AUTODESK INVENTOR PART (.ipt)
format: ipt  version: 2016 SP2 (Build 200236200, 236)  size: 8,607,232 bytes
history: native  units: mm
features: sketch x1
ambient origin geometry x8: Origin, YZ Plane, XZ Plane, XY Plane, X Axis, Y Axis, Z Axis, Center Point
bodies: Solid1 (feature_tree), Solid2 (feature_tree), Solid3 (feature_tree), Solid4 (feature_tree), Solid5 (feature_tree), Solid6 (feature_tree), Solid7 (feature_tree), Solid8 (feature_tree), Solid9 (feature_tree), Solid10 (feature_tree), Solid11 (feature_tree), Solid12 (feature_tree), Solid13 (feature_tree), Solid14 (feature_tree), Solid15 (feature_tree), Solid16 (feature_tree), Solid17 (feature_tree), Solid18 (feature_tree), Solid19 (feature_tree), Solid20 (feature_tree), Solid21 (feature_tree), Solid22 (feature_tree), Solid23 (feature_tree), Solid24 (feature_tree), Solid25 (feature_tree), Solid26 (feature_tree), Solid27 (feature_tree), Solid28 (feature_tree), Solid29 (feature_tree), Solid30 (feature_tree), Solid31 (feature_tree), Solid32 (feature_tree), Solid33 (feature_tree), Solid34 (feature_tree), Solid35 (feature_tree), Solid36 (feature_tree), Solid37 (feature_tree), Solid38 (feature_tree), Solid39 (feature_tree), Solid40 (feature_tree), Solid41 (feature_tree), Solid42 (feature_tree), Solid43 (feature_tree), Solid44 (feature_tree), Solid45 (feature_tree), Solid46 (feature_tree), Solid47 (feature_tree), Solid48 (feature_tree), Solid49 (feature_tree), Solid50 (feature_tree), Solid51 (feature_tree), Solid52 (feature_tree), Solid53 (feature_tree), Solid54 (feature_tree), Solid55 (feature_tree), Solid56 (feature_tree), Solid57 (feature_tree), Solid58 (feature_tree), Solid59 (feature_tree), Solid60 (feature_tree), Solid61 (feature_tree), Solid62 (feature_tree), Solid63 (feature_tree), Solid64 (feature_tree), Solid65 (feature_tree), Solid66 (feature_tree), Solid67 (feature_tree), Solid68 (feature_tree), Solid69 (feature_tree), Solid70 (feature_tree), Solid71 (feature_tree), Solid72 (feature_tree), Solid73 (feature_tree), Solid74 (feature_tree), Solid75 (feature_tree), Solid76 (feature_tree), Solid77 (feature_tree), Solid78 (feature_tree), Solid79 (feature_tree), Solid80 (feature_tree), Solid81 (feature_tree), Solid82 (feature_tree), Solid83 (feature_tree), Solid84 (feature_tree), Solid85 (feature_tree), Solid86 (feature_tree), Solid87 (feature_tree), Solid88 (feature_tree), Solid89 (feature_tree), Solid90 (feature_tree), Solid91 (feature_tree), Solid92 (feature_tree), Solid93 (feature_tree), Solid94 (feature_tree), Solid95 (feature_tree), Solid96 (feature_tree), Solid97 (feature_tree), Solid98 (feature_tree), Solid99 (feature_tree), Solid100 (feature_tree), Solid101 (feature_tree), Solid102 (feature_tree), Solid103 (feature_tree), Solid104 (feature_tree), Solid105 (feature_tree), Solid106 (feature_tree), Solid107 (feature_tree), Solid108 (feature_tree), Solid109 (feature_tree), Solid110 (feature_tree), Solid111 (feature_tree), Solid112 (feature_tree), Solid113 (feature_tree), Solid114 (feature_tree), Solid115 (feature_tree), Solid116 (feature_tree), Solid117 (feature_tree), Solid118 (feature_tree), Solid119 (feature_tree), Solid120 (feature_tree), Solid121 (feature_tree), Solid122 (feature_tree), Solid123 (feature_tree), Solid124 (feature_tree), Solid125 (feature_tree), Solid126 (feature_tree), Solid127 (feature_tree), Solid128 (feature_tree), Solid129 (feature_tree), Solid130 (feature_tree), Solid131 (feature_tree), Solid132 (feature_tree), Solid133 (feature_tree), Solid134 (feature_tree), Solid135 (feature_tree), Solid136 (feature_tree), Solid137 (feature_tree), Solid138 (feature_tree), Solid139 (feature_tree), Solid140 (feature_tree), Solid141 (feature_tree), Solid142 (feature_tree), Solid143 (feature_tree), Solid144 (feature_tree), Solid145 (feature_tree), Solid146 (feature_tree), Solid147 (feature_tree), Solid148 (feature_tree), Solid149 (feature_tree), Solid150 (feature_tree), Solid151 (feature_tree), Solid152 (feature_tree), Solid153 (feature_tree), Solid154 (feature_tree), Solid155 (feature_tree), Solid156 (feature_tree), Solid157 (feature_tree), Solid158 (feature_tree), Solid159 (feature_tree), Solid160 (feature_tree), Solid161 (feature_tree), Solid162 (feature_tree), Solid163 (feature_tree), Solid164 (feature_tree), Solid165 (feature_tree), Solid166 (feature_tree), Solid167 (feature_tree), Solid168 (feature_tree), Solid169 (feature_tree), Solid170 (feature_tree), Solid171 (feature_tree), Solid172 (feature_tree), Solid173 (feature_tree), Solid174 (feature_tree), Solid175 (feature_tree), Solid176 (feature_tree), Solid177 (feature_tree), Solid178 (feature_tree), Solid179 (feature_tree), Solid180 (feature_tree), Solid181 (feature_tree), Solid182 (feature_tree), Solid183 (feature_tree), Solid184 (feature_tree), Solid185 (feature_tree), Solid186 (feature_tree), Solid187 (feature_tree), Solid188 (feature_tree), Solid189 (feature_tree), Solid190 (feature_tree), Solid191 (feature_tree), Solid192 (feature_tree), Solid193 (feature_tree), Solid194 (feature_tree), Solid195 (feature_tree), Solid196 (feature_tree), Solid197 (feature_tree), Solid198 (feature_tree), Solid199 (feature_tree), Solid200 (feature_tree), Solid201 (feature_tree), Solid202 (feature_tree), Solid203 (feature_tree), Solid204 (feature_tree), Solid205 (feature_tree), Solid206 (feature_tree), Solid207 (feature_tree), Solid208 (feature_tree), Solid209 (feature_tree), Solid210 (feature_tree), Solid211 (feature_tree), Solid212 (feature_tree), Solid213 (feature_tree), Solid214 (feature_tree), Solid215 (feature_tree), Solid216 (feature_tree), Solid217 (feature_tree), Solid218 (feature_tree), Solid219 (feature_tree), Solid220 (feature_tree), Solid221 (feature_tree), Solid222 (feature_tree), Solid223 (feature_tree), Solid224 (feature_tree), Solid225 (feature_tree), Solid226 (feature_tree), Solid227 (feature_tree), Solid228 (feature_tree), Solid229 (feature_tree), Solid230 (feature_tree), Solid231 (feature_tree), Solid232 (feature_tree), Solid233 (feature_tree), Solid234 (feature_tree), Solid235 (feature_tree), Solid236 (feature_tree), Solid237 (feature_tree), Solid238 (feature_tree), Solid239 (feature_tree), Solid240 (feature_tree), Solid241 (feature_tree), Solid242 (feature_tree), Solid243 (feature_tree), Solid244 (feature_tree), Solid245 (feature_tree), Solid246 (feature_tree), Solid247 (feature_tree), Solid248 (feature_tree), Solid249 (feature_tree), Solid250 (feature_tree), Solid251 (feature_tree), Solid252 (feature_tree), Solid253 (feature_tree), Solid254 (feature_tree), Solid255 (feature_tree), Solid256 (feature_tree), Solid257 (feature_tree), Solid258 (feature_tree), Solid259 (feature_tree), Solid260 (feature_tree), Solid261 (feature_tree), Solid262 (feature_tree), Solid263 (feature_tree), Solid264 (feature_tree), Solid265 (feature_tree), Solid266 (feature_tree), Solid267 (feature_tree), Solid268 (feature_tree), Solid269 (feature_tree), Solid270 (feature_tree), Solid271 (feature_tree), Solid272 (feature_tree), Solid273 (feature_tree), Solid274 (feature_tree), Solid275 (feature_tree), Solid276 (feature_tree), Solid277 (feature_tree), Solid278 (feature_tree), Solid279 (feature_tree), Solid280 (feature_tree), Solid281 (feature_tree), Solid282 (feature_tree), Solid283 (feature_tree), Solid284 (feature_tree), Solid285 (feature_tree), Solid286 (feature_tree), Solid287 (feature_tree), Solid288 (feature_tree), Solid289 (feature_tree), Solid290 (feature_tree), Solid291 (feature_tree), Solid292 (feature_tree), Solid293 (feature_tree), Solid294 (feature_tree), Solid295 (feature_tree), Solid296 (feature_tree), Solid297 (feature_tree), Solid298 (feature_tree), Solid299 (feature_tree), Solid300 (feature_tree), Solid301 (feature_tree), Solid302 (feature_tree), Solid303 (feature_tree), Solid304 (feature_tree), Solid305 (feature_tree), Solid306 (feature_tree), Solid307 (feature_tree), Solid308 (feature_tree), Solid309 (feature_tree), Solid310 (feature_tree), Solid311 (feature_tree), Solid312 (feature_tree), Solid313 (feature_tree), Solid314 (feature_tree), Solid315 (feature_tree), Solid316 (feature_tree), Solid317 (feature_tree), Solid318 (feature_tree), Solid319 (feature_tree), Solid320 (feature_tree), Solid321 (feature_tree), Solid322 (feature_tree), Solid323 (feature_tree), Solid324 (feature_tree), Solid325 (feature_tree), Solid326 (feature_tree), Solid327 (feature_tree), Solid328 (feature_tree), Solid329 (feature_tree), Solid330 (feature_tree), Solid331 (feature_tree), Solid332 (feature_tree), Solid333 (feature_tree), Solid334 (feature_tree), Solid335 (feature_tree), Solid336 (feature_tree), Solid337 (feature_tree), Solid338 (feature_tree), Solid339 (feature_tree), Solid340 (feature_tree), Solid341 (feature_tree), Solid342 (feature_tree), Solid343 (feature_tree), Solid344 (feature_tree), Solid345 (feature_tree), Solid346 (feature_tree), Solid347 (feature_tree), Solid348 (feature_tree), Solid349 (feature_tree), Solid350 (feature_tree), Solid351 (feature_tree), Solid352 (feature_tree), Solid353 (feature_tree), Solid354 (feature_tree), Solid355 (feature_tree), Solid356 (feature_tree), Solid357 (feature_tree), Solid358 (feature_tree), Solid359 (feature_tree), Solid360 (feature_tree), Solid361 (feature_tree), Solid362 (feature_tree), Solid363 (feature_tree), Solid364 (feature_tree), Solid365 (feature_tree), Solid366 (feature_tree), Solid367 (feature_tree), Solid368 (feature_tree), Solid369 (feature_tree), Solid370 (feature_tree), Solid371 (feature_tree), Solid372 (feature_tree), Solid373 (feature_tree), Solid374 (feature_tree), Solid375 (feature_tree), Solid376 (feature_tree), Solid377 (feature_tree), Solid378 (feature_tree), Solid379 (feature_tree), Solid380 (feature_tree), Solid381 (feature_tree), Solid382 (feature_tree), Solid383 (feature_tree), Solid384 (feature_tree), Solid385 (feature_tree), Solid386 (feature_tree), Solid387 (feature_tree), Solid388 (feature_tree), Solid389 (feature_tree), Solid390 (feature_tree), Solid391 (feature_tree), Solid392 (feature_tree), Solid393 (feature_tree), Solid394 (feature_tree), Solid395 (feature_tree), Solid396 (feature_tree), Solid397 (feature_tree), Solid398 (feature_tree), Solid399 (feature_tree), Solid400 (feature_tree), Solid401 (feature_tree), Solid402 (feature_tree), Solid403 (feature_tree), Solid404 (feature_tree), Solid405 (feature_tree), Solid406 (feature_tree), Solid407 (feature_tree), Solid408 (feature_tree), Solid409 (feature_tree), Solid410 (feature_tree), Solid411 (feature_tree), Solid412 (feature_tree), Solid413 (feature_tree), Solid414 (feature_tree), Solid415 (feature_tree), Solid416 (feature_tree), Solid417 (feature_tree), Solid418 (feature_tree), Solid419 (feature_tree), Solid420 (feature_tree), Solid421 (feature_tree), Solid422 (feature_tree), Solid423 (feature_tree), Solid424 (feature_tree), Solid425 (feature_tree), Solid426 (feature_tree), Solid427 (feature_tree), Solid428 (feature_tree), Solid429 (feature_tree), Solid430 (feature_tree), Solid431 (feature_tree), Solid432 (feature_tree), Solid433 (feature_tree), Solid434 (feature_tree), Solid435 (feature_tree), Solid436 (feature_tree), Solid437 (feature_tree), Solid438 (feature_tree), Solid439 (feature_tree), Solid440 (feature_tree), Solid441 (feature_tree), Solid442 (feature_tree), Solid443 (feature_tree), Solid444 (feature_tree), Solid445 (feature_tree), Solid446 (feature_tree), Solid447 (feature_tree), Solid448 (feature_tree), Solid449 (feature_tree), Solid450 (feature_tree), Solid451 (feature_tree), Solid452 (feature_tree), Solid453 (feature_tree), Solid454 (feature_tree), Solid455 (feature_tree), Solid456 (feature_tree), Solid457 (feature_tree), Solid458 (feature_tree), Solid459 (feature_tree), Solid460 (feature_tree), Solid461 (feature_tree), Solid462 (feature_tree), Solid463 (feature_tree), Solid464 (feature_tree), Solid465 (feature_tree), Solid466 (feature_tree), Solid467 (feature_tree), Solid468 (feature_tree), Solid469 (feature_tree), Solid470 (feature_tree), Solid471 (feature_tree), Solid472 (feature_tree), Solid473 (feature_tree), Solid474 (feature_tree), Solid475 (feature_tree), Solid476 (feature_tree), Solid477 (feature_tree), Solid478 (feature_tree), Solid479 (feature_tree), Solid480 (feature_tree), Solid481 (feature_tree), Solid482 (feature_tree), Solid483 (feature_tree), Solid484 (feature_tree), Solid485 (feature_tree), Solid486 (feature_tree), Solid487 (feature_tree), Solid488 (feature_tree), Solid489 (feature_tree), Solid490 (feature_tree), Solid491 (feature_tree), Solid492 (feature_tree), Solid493 (feature_tree), Solid494 (feature_tree), Solid495 (feature_tree), Solid496 (feature_tree), Solid497 (feature_tree), Solid498 (feature_tree), Solid499 (feature_tree), Solid500 (feature_tree), Solid501 (feature_tree), Solid502 (feature_tree), Solid503 (feature_tree), Solid504 (feature_tree), Solid505 (feature_tree), Solid506 (feature_tree), Solid507 (feature_tree), Solid508 (feature_tree), Solid509 (feature_tree), Solid510 (feature_tree), Solid511 (feature_tree), Solid512 (feature_tree), Solid513 (feature_tree), Solid514 (feature_tree), Solid515 (feature_tree), Solid516 (feature_tree), Solid517 (feature_tree), Solid518 (feature_tree), Solid519 (feature_tree), Solid520 (feature_tree), Solid521 (feature_tree), Solid522 (feature_tree), Solid523 (feature_tree), Solid524 (feature_tree), Solid525 (feature_tree), Solid526 (feature_tree), Solid527 (feature_tree), Solid528 (feature_tree), Solid529 (feature_tree), Solid530 (feature_tree), Solid531 (feature_tree), Solid532 (feature_tree), Solid533 (feature_tree), Solid534 (feature_tree), Solid535 (feature_tree), Solid536 (feature_tree), Solid537 (feature_tree), Solid538 (feature_tree), Solid539 (feature_tree), Solid540 (feature_tree), Solid541 (feature_tree), Solid542 (feature_tree), Solid543 (feature_tree), Solid544 (feature_tree), Solid545 (feature_tree), Solid546 (feature_tree), Solid547 (feature_tree), Solid548 (feature_tree), Solid549 (feature_tree), Solid550 (feature_tree), Solid551 (feature_tree), Solid552 (feature_tree), Solid553 (feature_tree), Solid554 (feature_tree), Solid555 (feature_tree), Solid556 (feature_tree), Solid557 (feature_tree), Solid558 (feature_tree), Solid559 (feature_tree), Solid560 (feature_tree), Solid561 (feature_tree), Solid562 (feature_tree), Solid563 (feature_tree), Solid564 (feature_tree), Solid565 (feature_tree), Solid566 (feature_tree), Solid567 (feature_tree), Solid568 (feature_tree), Solid569 (feature_tree), Solid570 (feature_tree), Solid571 (feature_tree), Solid572 (feature_tree), Solid573 (feature_tree), Solid574 (feature_tree), Solid575 (feature_tree), Solid576 (feature_tree), Solid577 (feature_tree), Solid578 (feature_tree), Solid579 (feature_tree), Solid580 (feature_tree), Solid581 (feature_tree), Solid582 (feature_tree), Solid583 (feature_tree), Solid584 (feature_tree), Solid585 (feature_tree), Solid586 (feature_tree), Solid587 (feature_tree), Solid588 (feature_tree), Solid589 (feature_tree), Solid590 (feature_tree), Solid591 (feature_tree), Solid592 (feature_tree), Solid593 (feature_tree), Solid594 (feature_tree), Solid595 (feature_tree), Solid596 (feature_tree), Solid597 (feature_tree), Solid598 (feature_tree), Solid599 (feature_tree), Solid600 (feature_tree), Solid601 (feature_tree), Solid602 (feature_tree), Solid603 (feature_tree), Solid604 (feature_tree), Solid605 (feature_tree), Solid606 (feature_tree), Solid607 (feature_tree), Solid608 (feature_tree), Solid609 (feature_tree), Solid610 (feature_tree), Solid611 (feature_tree), Solid612 (feature_tree), Solid613 (feature_tree), Solid614 (feature_tree), Solid615 (feature_tree), Solid616 (feature_tree), Solid617 (feature_tree), Solid618 (feature_tree), Solid619 (feature_tree), Solid620 (feature_tree), Solid621 (feature_tree), Solid622 (feature_tree), Solid623 (feature_tree), Solid624 (feature_tree), Solid625 (feature_tree), Solid626 (feature_tree), Solid627 (feature_tree), Solid628 (feature_tree), Solid629 (feature_tree), Solid630 (feature_tree), Solid631 (feature_tree), Solid632 (feature_tree), Solid633 (feature_tree), Solid634 (feature_tree), Solid635 (feature_tree), Solid636 (feature_tree), Solid637 (feature_tree), Solid638 (feature_tree), Solid639 (feature_tree), Solid640 (feature_tree), Solid641 (feature_tree), Solid642 (feature_tree), Solid643 (feature_tree), Solid644 (feature_tree), Solid645 (feature_tree), Solid646 (feature_tree), Solid647 (feature_tree), Solid648 (feature_tree), Solid649 (feature_tree), Solid650 (feature_tree), Solid651 (feature_tree), Solid652 (feature_tree), Solid653 (feature_tree), Solid654 (feature_tree), Solid655 (feature_tree), Solid656 (feature_tree), Solid657 (feature_tree), Solid658 (feature_tree), Solid659 (feature_tree), Solid660 (feature_tree), Solid661 (feature_tree), Solid662 (feature_tree), Solid663 (feature_tree), Solid664 (feature_tree), Solid665 (feature_tree), Solid666 (feature_tree), Solid667 (feature_tree), Solid668 (feature_tree), Solid669 (feature_tree), Solid670 (feature_tree), Solid671 (feature_tree), Solid672 (feature_tree), Solid673 (feature_tree), Solid674 (feature_tree), Solid675 (feature_tree), Solid676 (feature_tree), Solid677 (feature_tree), Solid678 (feature_tree), Solid679 (feature_tree), Solid680 (feature_tree), Solid681 (feature_tree), Solid682 (feature_tree), Solid683 (feature_tree), Solid684 (feature_tree), Solid685 (feature_tree), Solid686 (feature_tree), Solid687 (feature_tree), Solid688 (feature_tree), Solid689 (feature_tree), Solid690 (feature_tree), Solid691 (feature_tree), Solid692 (feature_tree), Solid693 (feature_tree), Solid694 (feature_tree), Solid695 (feature_tree), Solid696 (feature_tree), Solid697 (feature_tree), Solid698 (feature_tree), Solid699 (feature_tree), Solid700 (feature_tree), Solid701 (feature_tree)
feature tree (1):
  sketch  "Sketch1"
